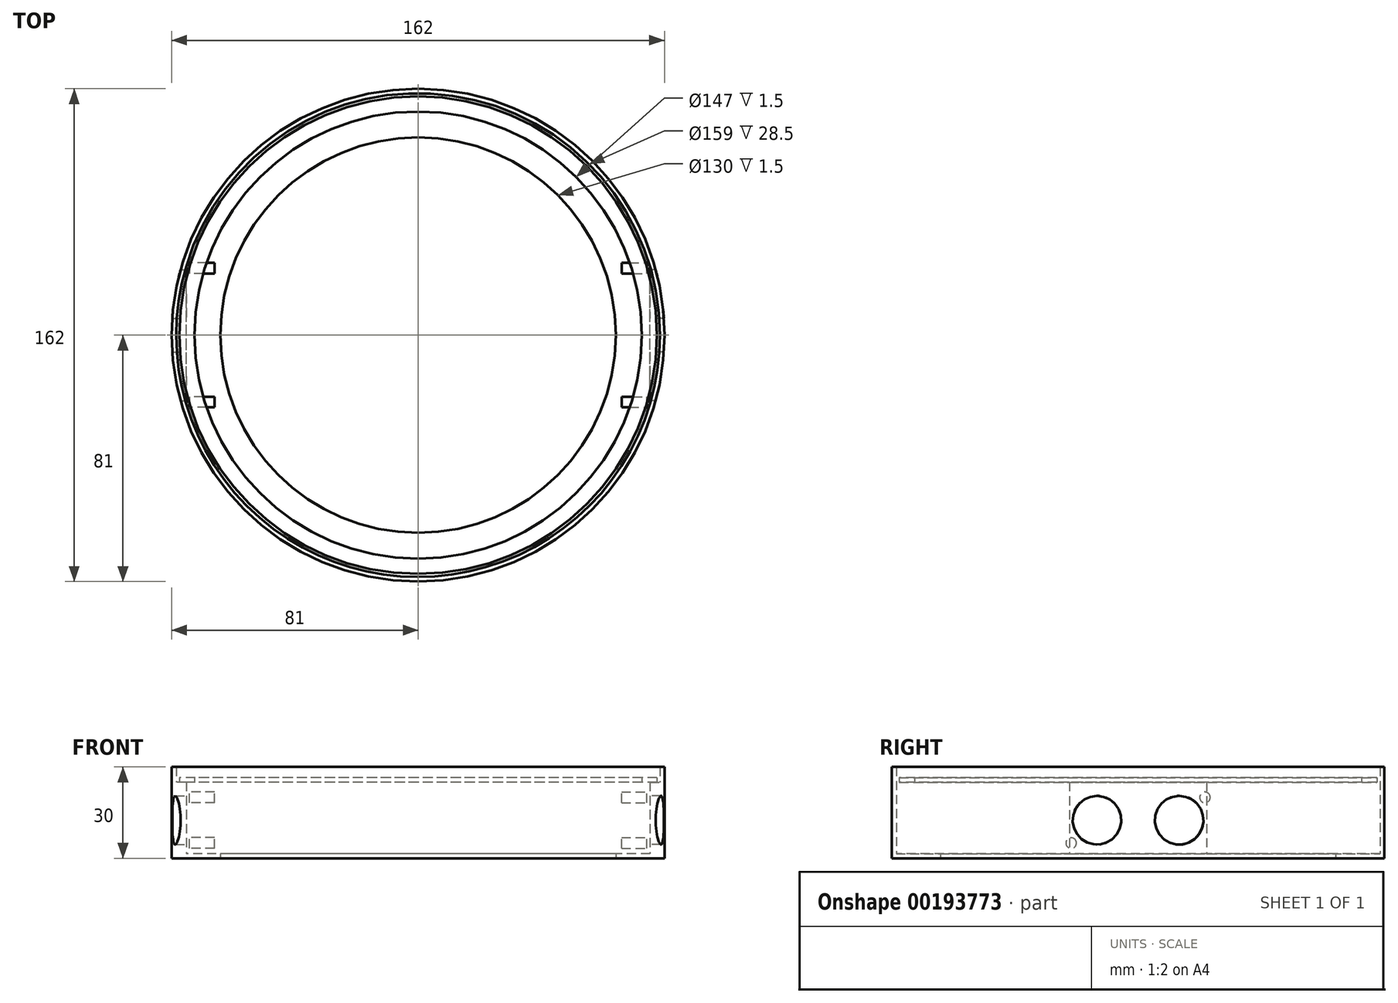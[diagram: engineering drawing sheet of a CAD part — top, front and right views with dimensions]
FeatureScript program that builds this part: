
annotation { "Feature Type Name" : "Feature", "Feature Type Description" : "" }
export const myFeature = defineFeature(function(context is Context, id is Id, definition is map)
    precondition{}
    {
        {
            var Q0;
            Q0=qCreatedBy(makeId("Top.planeOp"),FACE);
            var sketch = newSketch(context, id + "F0", { "sketchPlane" : qUnion([Q0])});
            skCircle(sketch, "E0", {"center": v(0, 0) * mm, "radius": 81 * mm});
            skCircle(sketch, "E1", {"center": v(0, 0) * mm, "radius": 79.5 * mm});
            skLineSegment(sketch, "E2", {"start": v(-76.25, -22.5) * mm, "end": v(-76.25, 22.5) * mm});
            skLineSegment(sketch, "E3", {"start": v(76.25, -22.49) * mm, "end": v(76.25, 22.49) * mm});
            skCircle(sketch, "E4", {"center": v(0, 0) * mm, "radius": 65 * mm});
            skSolve(sketch);
        }
        {
            var Q0;
            Q0=makeQuery(id+"F0.imprint","IMPRINT",FACE,{"disambiguationData":[TD([[makeQuery(id+"F0.imprint","IMPRINT",EDGE,{"derivedFrom":sQuery(id+"F0.wireOp",EDGE,"E0")}),1.0]])]});
            extrude(context, id + "F1", {"entities" : qUnion([Q0]), "depth" : 30 * mm});
        }
        {
            var Q0;
            Q0=qCreatedBy(makeId("Right.planeOp"),FACE);
            var sketch = newSketch(context, id + "F2", { "sketchPlane" : qUnion([Q0])});
            skCircle(sketch, "E5", {"center": v(-13.5, 12.5) * mm, "radius": 8.5 * mm});
            skCircle(sketch, "E6.1.0.0", {"center": v(13.5, 12.5) * mm, "radius": 8.5 * mm});
            skLineSegment(sketch, "E6.direction1", {"start": v(-13.5, 12.5) * mm, "end": v(13.5, 12.5) * mm, "construction": true});
            skCircle(sketch, "E7", {"center": v(22, 20) * mm, "radius": 1.75 * mm});
            skCircle(sketch, "E8.MirrorC", {"center": v(-22, 20) * mm, "radius": 1.75 * mm});
            skCircle(sketch, "E9.MirrorC", {"center": v(-22, 5) * mm, "radius": 1.75 * mm});
            skCircle(sketch, "E10.MirrorC", {"center": v(22, 5) * mm, "radius": 1.75 * mm});
            skSolve(sketch);
        }
        {
            var Q0;
            {var subQ0=sQuery(id+"F0.wireOp",EDGE,"E2");Q0=makeQuery(id+"F0.imprint","IMPRINT",FACE,{"disambiguationData":[TD([[makeQuery(id+"F0.imprint","IMPRINT",EDGE,{"derivedFrom":subQ0}),1.0]])]});}
            extrude(context, id + "F3", {"entities" : qUnion([Q0]), "operationType" : NewBodyOperationType.ADD, "depth" : 25 * mm});
        }
        {
            var Q0;
            {var subQ0=sQuery(id+"F0.wireOp",EDGE,"E3");Q0=makeQuery(id+"F0.imprint","IMPRINT",FACE,{"disambiguationData":[TD([[makeQuery(id+"F0.imprint","IMPRINT",EDGE,{"derivedFrom":subQ0}),-1.0]])]});}
            extrude(context, id + "F4", {"entities" : qUnion([Q0]), "operationType" : NewBodyOperationType.ADD, "depth" : 25 * mm});
        }
        {
            var Q0;
            Q0=sQuery(id+"F2.wireOp",VERTEX,"E5.center");
            var Q1;
            Q1=sQuery(id+"F2.wireOp",VERTEX,"E6.1.0.0.center");
            var Q2;
            Q2=makeQuery(id+"F1.opExtrude","SWEPT_BODY",BODY,{"disambiguationData":[OSD([sQuery(id+"F0.wireOp",EDGE,"E0"),sQuery(id+"F0.wireOp",EDGE,"E1")])]});
            hole(context, id + "F5", {"style" : HoleStyle.SIMPLE, "endStyle" : HoleEndStyle.THROUGH, "holeDiameter" : 16 * mm, "locations" : qUnion([Q0, Q1]), "scope" : qUnion([Q2]), "isTappedThrough" : true});
        }
        {
            var Q0;
            Q0=sQuery(id+"F2.wireOp",VERTEX,"E5.center");
            var Q1;
            Q1=sQuery(id+"F2.wireOp",VERTEX,"E6.1.0.0.center");
            var Q2;
            Q2=makeQuery(id+"F1.opExtrude","SWEPT_BODY",BODY,{"disambiguationData":[OSD([sQuery(id+"F0.wireOp",EDGE,"E0"),sQuery(id+"F0.wireOp",EDGE,"E1")])]});
            hole(context, id + "F6", {"style" : HoleStyle.SIMPLE, "endStyle" : HoleEndStyle.THROUGH, "oppositeDirection" : true, "holeDiameter" : 16 * mm, "locations" : qUnion([Q0, Q1]), "scope" : qUnion([Q2]), "isTappedThrough" : true});
        }
        {
            var Q0;
            {var subQ1=sQuery(id+"F0.wireOp",EDGE,"E2");Q0=makeQuery(id+"F0.imprint","IMPRINT",FACE,{"disambiguationData":[TD([[makeQuery(id+"F0.imprint","IMPRINT",EDGE,{"derivedFrom":subQ1}),-1.0]])]});}
            extrude(context, id + "F7", {"entities" : qUnion([Q0]), "operationType" : NewBodyOperationType.ADD, "depth" : 1.5 * mm});
        }
        {
            var Q0;
            Q0=makeQuery(id+"F2.imprint","IMPRINT",FACE,{"disambiguationData":[TD([[makeQuery(id+"F2.imprint","IMPRINT",EDGE,{"derivedFrom":sQuery(id+"F2.wireOp",EDGE,"E7")}),1.0]])]});
            var Q1;
            Q1=makeQuery(id+"F2.imprint","IMPRINT",FACE,{"disambiguationData":[TD([[makeQuery(id+"F2.imprint","IMPRINT",EDGE,{"derivedFrom":sQuery(id+"F2.wireOp",EDGE,"E10.MirrorC")}),-1.0]])]});
            var Q2;
            Q2=makeQuery(id+"F2.imprint","IMPRINT",FACE,{"disambiguationData":[TD([[makeQuery(id+"F2.imprint","IMPRINT",EDGE,{"derivedFrom":sQuery(id+"F2.wireOp",EDGE,"E9.MirrorC")}),1.0]])]});
            var Q3;
            Q3=makeQuery(id+"F2.imprint","IMPRINT",FACE,{"disambiguationData":[TD([[makeQuery(id+"F2.imprint","IMPRINT",EDGE,{"derivedFrom":sQuery(id+"F2.wireOp",EDGE,"E8.MirrorC")}),-1.0]])]});
            extrude(context, id + "F8", {"entities" : qUnion([Q0, Q1, Q2, Q3]), "depth" : 8.3 * mm});
        }
        {
            var Q0;
            Q0=makeQuery(id+"F8.opExtrude","SWEPT_BODY",BODY,{"disambiguationData":[OSD([sQuery(id+"F2.wireOp",EDGE,"E8.MirrorC")])]});
            var Q1;
            Q1=makeQuery(id+"F8.opExtrude","SWEPT_BODY",BODY,{"disambiguationData":[OSD([sQuery(id+"F2.wireOp",EDGE,"E9.MirrorC")])]});
            var Q2;
            Q2=makeQuery(id+"F8.opExtrude","SWEPT_BODY",BODY,{"disambiguationData":[OSD([sQuery(id+"F2.wireOp",EDGE,"E10.MirrorC")])]});
            var Q3;
            Q3=makeQuery(id+"F8.opExtrude","SWEPT_BODY",BODY,{"disambiguationData":[OSD([sQuery(id+"F2.wireOp",EDGE,"E7")])]});
            var Q4;
            Q4=makeQuery(id+"F3.opExtrude","SWEPT_FACE",FACE,{"disambiguationData":[OSD([sQuery(id+"F0.wireOp",EDGE,"E2")])]});
            transform(context, id + "F9", {"entities" : qUnion([Q0, Q1, Q2, Q3]), "transformType" : TransformType.TRANSLATION_DISTANCE, "transformDirection" : qUnion([Q4]), "distance" : 75.2 * mm, "oppositeDirection" : true, "makeCopy" : false});
        }
        {
            var Q0;
            Q0=makeQuery(id+"F2.imprint","IMPRINT",FACE,{"disambiguationData":[TD([[makeQuery(id+"F2.imprint","IMPRINT",EDGE,{"derivedFrom":sQuery(id+"F2.wireOp",EDGE,"E8.MirrorC")}),-1.0]])]});
            var Q1;
            Q1=makeQuery(id+"F2.imprint","IMPRINT",FACE,{"disambiguationData":[TD([[makeQuery(id+"F2.imprint","IMPRINT",EDGE,{"derivedFrom":sQuery(id+"F2.wireOp",EDGE,"E9.MirrorC")}),1.0]])]});
            var Q2;
            Q2=makeQuery(id+"F2.imprint","IMPRINT",FACE,{"disambiguationData":[TD([[makeQuery(id+"F2.imprint","IMPRINT",EDGE,{"derivedFrom":sQuery(id+"F2.wireOp",EDGE,"E10.MirrorC")}),-1.0]])]});
            var Q3;
            Q3=makeQuery(id+"F2.imprint","IMPRINT",FACE,{"disambiguationData":[TD([[makeQuery(id+"F2.imprint","IMPRINT",EDGE,{"derivedFrom":sQuery(id+"F2.wireOp",EDGE,"E7")}),1.0]])]});
            extrude(context, id + "F10", {"entities" : qUnion([Q0, Q1, Q2, Q3]), "oppositeDirection" : true, "depth" : 8.3 * mm});
        }
        {
            var Q0;
            Q0=makeQuery(id+"F10.opExtrude","SWEPT_BODY",BODY,{"disambiguationData":[OSD([sQuery(id+"F2.wireOp",EDGE,"E8.MirrorC")])]});
            var Q1;
            Q1=makeQuery(id+"F10.opExtrude","SWEPT_BODY",BODY,{"disambiguationData":[OSD([sQuery(id+"F2.wireOp",EDGE,"E9.MirrorC")])]});
            var Q2;
            Q2=makeQuery(id+"F10.opExtrude","SWEPT_BODY",BODY,{"disambiguationData":[OSD([sQuery(id+"F2.wireOp",EDGE,"E7")])]});
            var Q3;
            Q3=makeQuery(id+"F10.opExtrude","SWEPT_BODY",BODY,{"disambiguationData":[OSD([sQuery(id+"F2.wireOp",EDGE,"E10.MirrorC")])]});
            var Q4;
            Q4=makeQuery(id+"F4.opExtrude","SWEPT_FACE",FACE,{"disambiguationData":[OSD([sQuery(id+"F0.wireOp",EDGE,"E3")])]});
            transform(context, id + "F11", {"entities" : qUnion([Q0, Q1, Q2, Q3]), "transformType" : TransformType.TRANSLATION_DISTANCE, "transformDirection" : qUnion([Q4]), "distance" : 75.2 * mm, "oppositeDirection" : true, "makeCopy" : false});
        }
        {
            var Q0;
            Q0=qCreatedBy(makeId("Top.planeOp"),FACE);
            var sketch = newSketch(context, id + "F12", { "sketchPlane" : qUnion([Q0])});
            skCircle(sketch, "E11", {"center": v(0, 0) * mm, "radius": 73.5 * mm});
            skCircle(sketch, "E12", {"center": v(0, 0) * mm, "radius": 78.5 * mm});
            skSolve(sketch);
        }
        {
            var Q0;
            Q0=makeQuery(id+"F12.imprint","IMPRINT",FACE,{"disambiguationData":[TD([[makeQuery(id+"F12.imprint","IMPRINT",EDGE,{"derivedFrom":sQuery(id+"F12.wireOp",EDGE,"E11")}),-1.0]])]});
            extrude(context, id + "F13", {"entities" : qUnion([Q0]), "depth" : 1.5 * mm});
        }
        {
            var Q0;
            Q0=makeQuery(id+"F13.opExtrude","SWEPT_BODY",BODY,{"disambiguationData":[OSD([sQuery(id+"F12.wireOp",EDGE,"E11"),sQuery(id+"F12.wireOp",EDGE,"E12")])]});
            var Q1;
            Q1=qCreatedBy(makeId("Top.planeOp"),FACE);
            transform(context, id + "F14", {"entities" : qUnion([Q0]), "transformType" : TransformType.TRANSLATION_DISTANCE, "transformDirection" : qUnion([Q1]), "distance" : 25 * mm, "makeCopy" : false});
        }
    });
